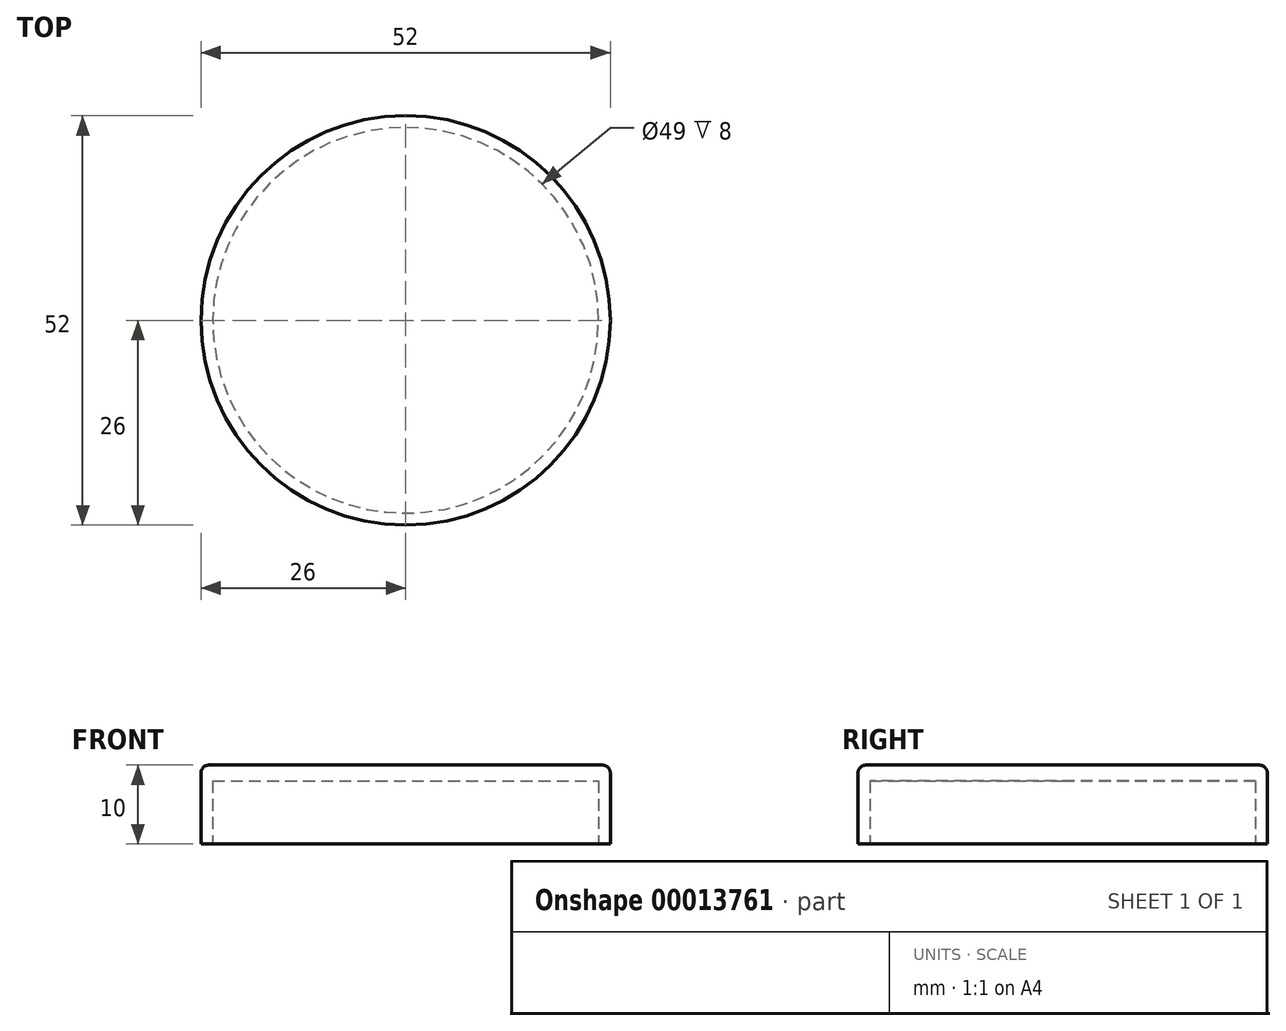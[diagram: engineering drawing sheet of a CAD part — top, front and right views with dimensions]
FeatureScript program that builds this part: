
annotation { "Feature Type Name" : "Feature", "Feature Type Description" : "" }
export const myFeature = defineFeature(function(context is Context, id is Id, definition is map)
    precondition{}
    {
        {
            var Q0;
            Q0=qCreatedBy(makeId("Top.planeOp"),FACE);
            var sketch = newSketch(context, id + "F0", { "sketchPlane" : qUnion([Q0])});
            skCircle(sketch, "E0", {"center": v(0, 0) * mm, "radius": 26 * mm});
            skSolve(sketch);
        }
        {
            var Q0;
            Q0=makeQuery(id+"F0.imprint","IMPRINT",FACE,{"disambiguationData":[TD([[makeQuery(id+"F0.imprint","IMPRINT",EDGE,{"derivedFrom":sQuery(id+"F0.wireOp",EDGE,"E0")}),1.0]])]});
            extrude(context, id + "F1", {"entities" : qUnion([Q0]), "depth" : 10 * mm});
        }
        {
            var Q0;
            Q0=makeQuery(id+"F1.opExtrude","CAP_FACE",FACE,{"disambiguationData":[OSD([sQuery(id+"F0.wireOp",EDGE,"E0")])],"isStart":true});
            var sketch = newSketch(context, id + "F2", { "sketchPlane" : qUnion([Q0])});
            skCircle(sketch, "E1", {"center": v(0, 0) * mm, "radius": 24.5 * mm});
            skSolve(sketch);
        }
        {
            var Q0;
            Q0=makeQuery(id+"F2.imprint","IMPRINT",FACE,{"disambiguationData":[TD([[makeQuery(id+"F2.imprint","IMPRINT",EDGE,{"derivedFrom":sQuery(id+"F2.wireOp",EDGE,"E1")}),1.0]])]});
            extrude(context, id + "F3", {"entities" : qUnion([Q0]), "operationType" : NewBodyOperationType.REMOVE, "oppositeDirection" : true, "depth" : 8 * mm});
        }
        {
            var Q0;
            Q0=makeQuery(id+"F1.opExtrude","CAP_EDGE",EDGE,{"disambiguationData":[OSD([sQuery(id+"F0.wireOp",EDGE,"E0")])],"isStart":false});
            fillet(context, id + "F4", {"entities" : qUnion([Q0]), "radius" : 1 * mm, "tangentPropagation" : true, "allowEdgeOverflow" : false});
        }
    });
